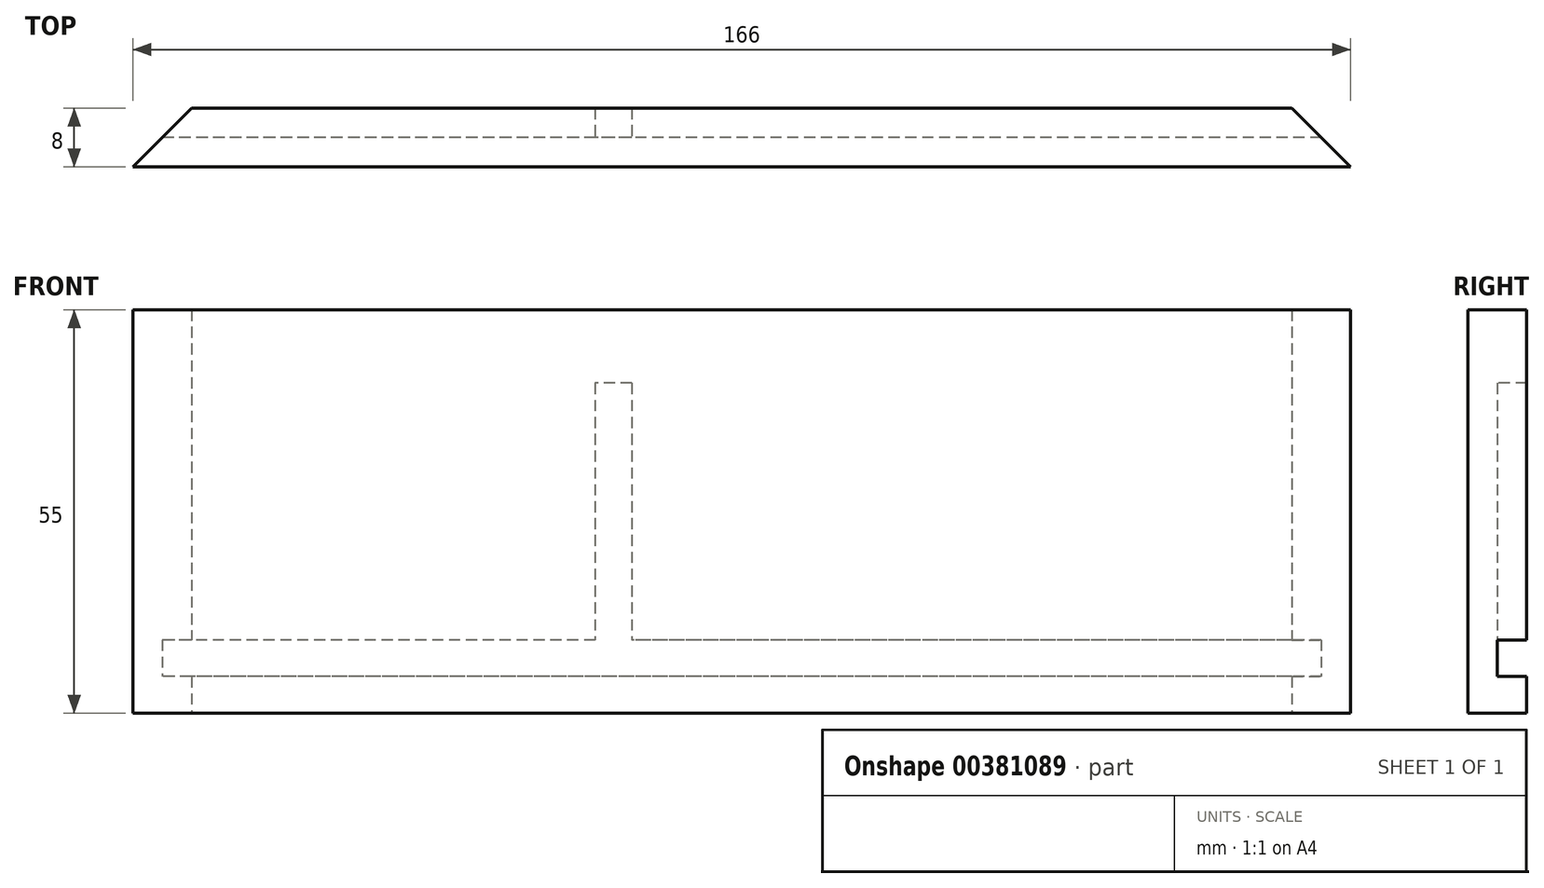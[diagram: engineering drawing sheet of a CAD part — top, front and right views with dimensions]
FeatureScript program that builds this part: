
annotation { "Feature Type Name" : "Feature", "Feature Type Description" : "" }
export const myFeature = defineFeature(function(context is Context, id is Id, definition is map)
    precondition{}
    {
        {
            var Q0;
            Q0=qCreatedBy(makeId("Top.planeOp"),FACE);
            var sketch = newSketch(context, id + "F0", { "sketchPlane" : qUnion([Q0])});
            skLineSegment(sketch, "E0.bottom", {"start": v(-83, -4) * mm, "end": v(83, -4) * mm});
            skLineSegment(sketch, "E1", {"start": v(-75, 4) * mm, "end": v(-83, -4) * mm});
            skLineSegment(sketch, "E2", {"start": v(75, 4) * mm, "end": v(83, -4) * mm});
            skLineSegment(sketch, "E3", {"start": v(-75, 4) * mm, "end": v(75, 4) * mm});
            skSolve(sketch);
        }
        {
            var Q0;
            Q0=makeQuery(id+"F0.imprint","IMPRINT",FACE,{"disambiguationData":[TD([[makeQuery(id+"F0.imprint","IMPRINT",EDGE,{"derivedFrom":sQuery(id+"F0.wireOp",EDGE,"E0.bottom")}),1.0]])]});
            extrude(context, id + "F1", {"entities" : qUnion([Q0]), "depth" : 55 * mm});
        }
        {
            var Q0;
            Q0=qCreatedBy(makeId("Right.planeOp"),FACE);
            var sketch = newSketch(context, id + "F2", { "sketchPlane" : qUnion([Q0])});
            skLineSegment(sketch, "E4.bottom", {"start": v(0, 5) * mm, "end": v(4, 5) * mm});
            skLineSegment(sketch, "E4.top", {"start": v(0, 10) * mm, "end": v(4, 10) * mm});
            skLineSegment(sketch, "E4.left", {"start": v(0, 5) * mm, "end": v(0, 10) * mm});
            skLineSegment(sketch, "E4.right", {"start": v(4, 5) * mm, "end": v(4, 10) * mm});
            skSolve(sketch);
        }
        {
            var Q0;
            Q0=qSketchRegion(id+"F2",true);
            extrude(context, id + "F3", {"entities" : qUnion([Q0]), "operationType" : NewBodyOperationType.REMOVE, "endBound" : BoundingType.SYMMETRIC, "depth" : 166 * mm});
        }
        {
            var Q0;
            Q0=qCreatedBy(makeId("Front.planeOp"),FACE);
            var sketch = newSketch(context, id + "F4", { "sketchPlane" : qUnion([Q0])});
            skLineSegment(sketch, "E5.bottom", {"start": v(-15, 45) * mm, "end": v(-20, 45) * mm});
            skLineSegment(sketch, "E5.top", {"start": v(-15, 10) * mm, "end": v(-20, 10) * mm});
            skLineSegment(sketch, "E5.left", {"start": v(-15, 45) * mm, "end": v(-15, 10) * mm});
            skLineSegment(sketch, "E5.right", {"start": v(-20, 45) * mm, "end": v(-20, 10) * mm});
            skSolve(sketch);
        }
        {
            var Q0;
            Q0 = qSketchRegion(id + "F4", true);
            extrude(context, id + "F5", {"entities" : qUnion([Q0]), "operationType" : NewBodyOperationType.REMOVE, "oppositeDirection" : true, "depth" : 4 * mm});
        }
    });
